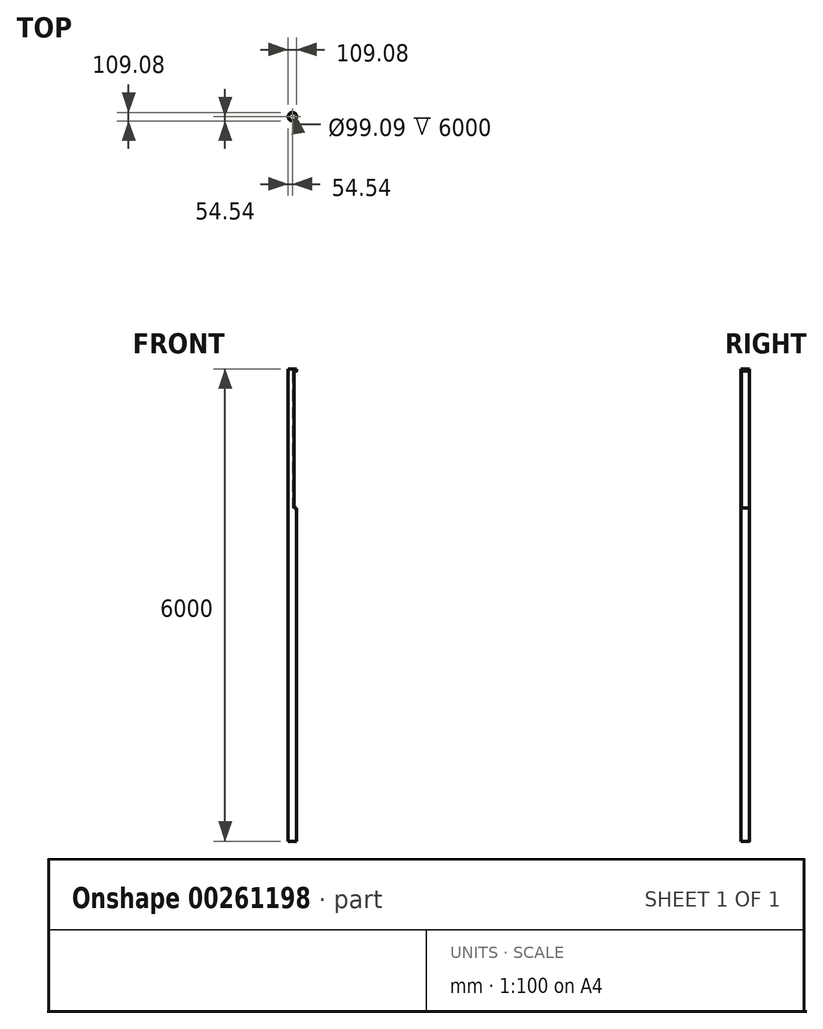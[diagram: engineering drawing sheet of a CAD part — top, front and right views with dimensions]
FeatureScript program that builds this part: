
annotation { "Feature Type Name" : "Feature", "Feature Type Description" : "" }
export const myFeature = defineFeature(function(context is Context, id is Id, definition is map)
    precondition{}
    {
        {
            var Q0;
            Q0=qCreatedBy(makeId("Top.planeOp"),FACE);
            var sketch = newSketch(context, id + "F0", { "sketchPlane" : qUnion([Q0])});
            skCircle(sketch, "E0", {"center": v(0, 0) * mm, "radius": 54.54 * mm});
            skSolve(sketch);
        }
        {
            var Q0;
            Q0 = qSketchRegion(id + "F0", true);
            extrude(context, id + "F1", {"entities" : qUnion([Q0]), "depth" : 6000 * mm});
        }
        {
            var Q0;
            Q0=makeQuery(id+"F1.opExtrude","CAP_FACE",FACE,{"disambiguationData":[OSD([sQuery(id+"F0.wireOp",EDGE,"E0")])],"isStart":false});
            var Q1;
            Q1=makeQuery(id+"F1.opExtrude","CAP_FACE",FACE,{"disambiguationData":[OSD([sQuery(id+"F0.wireOp",EDGE,"E0")])],"isStart":true});
            shell(context, id + "F2", {"entities" : qUnion([Q0, Q1]), "thickness" : 5 * mm});
        }
        {
            var Q0;
            Q0=qCreatedBy(makeId("Right.planeOp"),FACE);
            var sketch = newSketch(context, id + "F3", { "sketchPlane" : qUnion([Q0])});
            skLineSegment(sketch, "E1.bottom", {"start": v(-51.76, 5971.43) * mm, "end": v(51.76, 5971.43) * mm});
            skLineSegment(sketch, "E1.top", {"start": v(-51.76, 4230.4) * mm, "end": v(51.76, 4230.4) * mm});
            skLineSegment(sketch, "E1.left", {"start": v(-51.76, 5971.43) * mm, "end": v(-51.76, 4230.4) * mm});
            skLineSegment(sketch, "E1.right", {"start": v(51.76, 5971.43) * mm, "end": v(51.76, 4230.4) * mm});
            skPoint(sketch, "E1.middle", {"position": v(0, 5100.91) * mm});
            skSolve(sketch);
        }
        {
            var Q0;
            Q0 = qSketchRegion(id + "F3", true);
            extrude(context, id + "F4", {"entities" : qUnion([Q0]), "operationType" : NewBodyOperationType.REMOVE, "depth" : 772.16 * mm});
        }
    });
